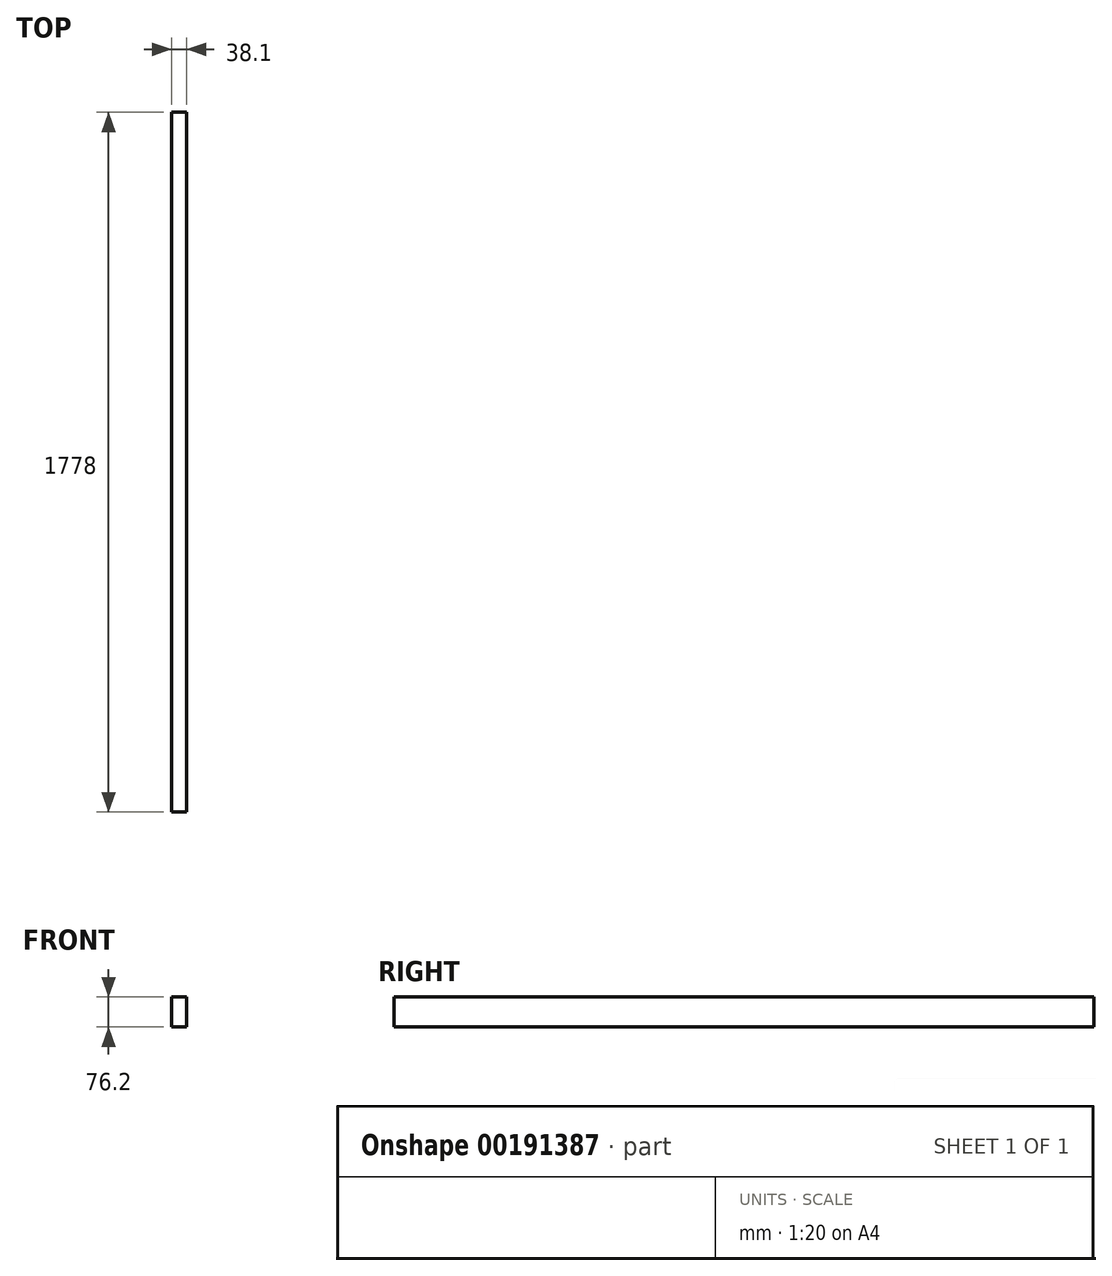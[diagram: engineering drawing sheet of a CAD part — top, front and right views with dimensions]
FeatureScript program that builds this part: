
annotation { "Feature Type Name" : "Feature", "Feature Type Description" : "" }
export const myFeature = defineFeature(function(context is Context, id is Id, definition is map)
    precondition{}
    {
        {
            var Q0;
            Q0=qCreatedBy(makeId("Front.planeOp"),FACE);
            var sketch = newSketch(context, id + "F0", { "sketchPlane" : qUnion([Q0])});
            skLineSegment(sketch, "E0.bottom", {"start": v(-19.05, 38.1) * mm, "end": v(19.05, 38.1) * mm});
            skLineSegment(sketch, "E0.top", {"start": v(-19.05, -38.1) * mm, "end": v(19.05, -38.1) * mm});
            skLineSegment(sketch, "E0.left", {"start": v(-19.05, 38.1) * mm, "end": v(-19.05, -38.1) * mm});
            skLineSegment(sketch, "E0.right", {"start": v(19.05, 38.1) * mm, "end": v(19.05, -38.1) * mm});
            skLineSegment(sketch, "E1", {"start": v(19.05, 38.1) * mm, "end": v(-19.05, -38.1) * mm, "construction": true});
            skSolve(sketch);
        }
        {
            var Q0;
            Q0=makeQuery(id+"F0.imprint","IMPRINT",FACE,{"disambiguationData":[TD([[makeQuery(id+"F0.imprint","IMPRINT",EDGE,{"derivedFrom":sQuery(id+"F0.wireOp",EDGE,"E0.bottom")}),-1.0]])]});
            extrude(context, id + "F1", {"entities" : qUnion([Q0]), "depth" : 1778 * mm});
        }
    });
